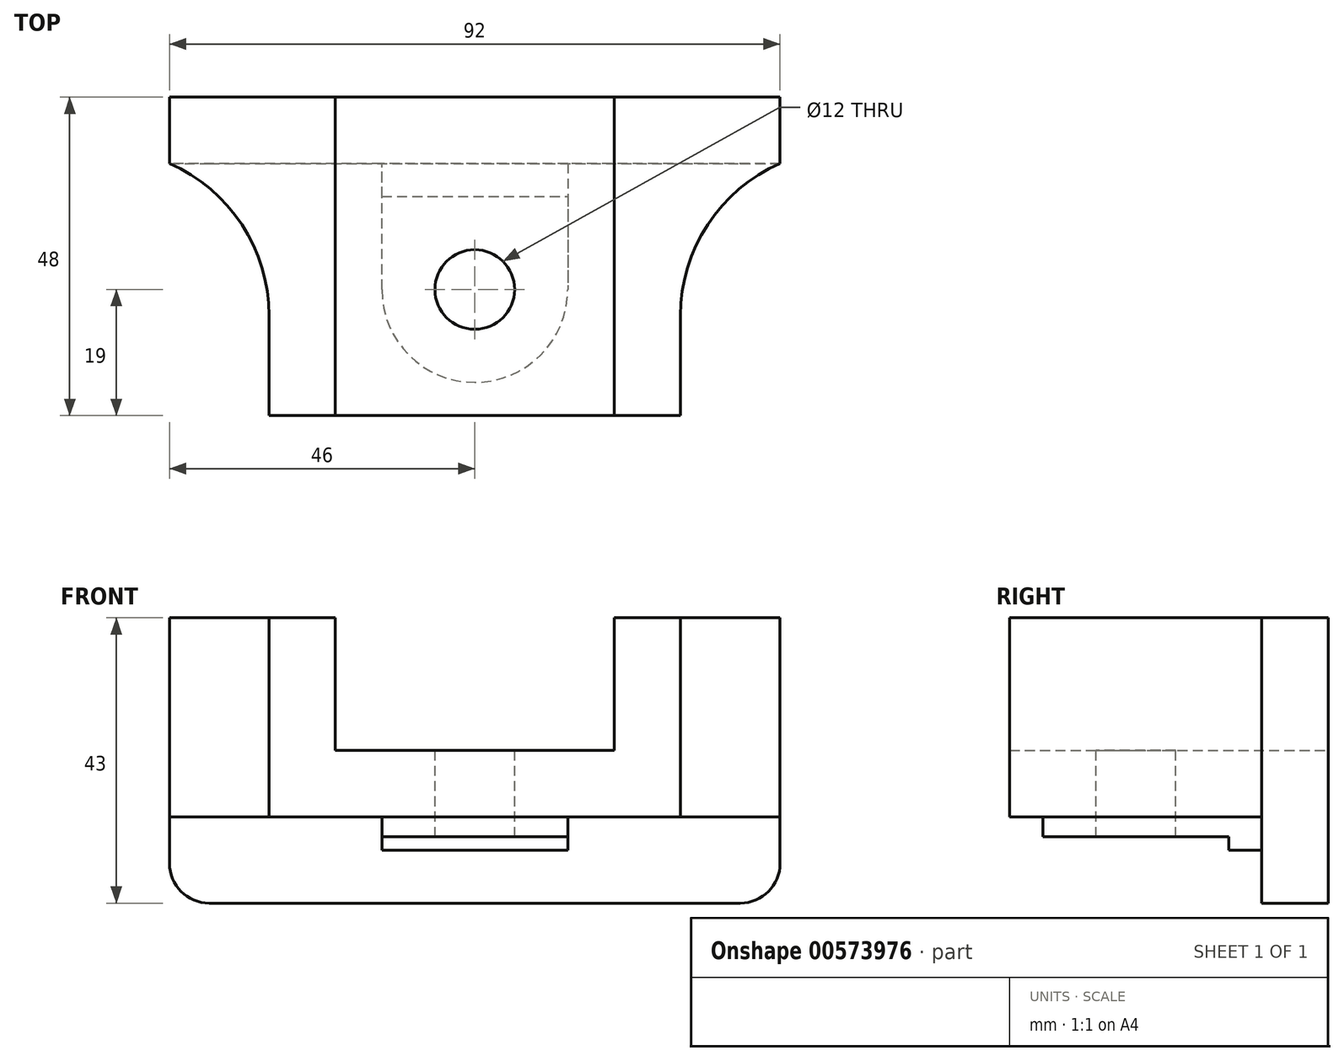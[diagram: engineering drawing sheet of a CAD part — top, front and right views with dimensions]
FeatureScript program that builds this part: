
annotation { "Feature Type Name" : "Feature", "Feature Type Description" : "" }
export const myFeature = defineFeature(function(context is Context, id is Id, definition is map)
    precondition{}
    {
        {
            var Q0;
            Q0=qCreatedBy(makeId("Front.planeOp"),FACE);
            var sketch = newSketch(context, id + "F0", { "sketchPlane" : qUnion([Q0])});
            skLineSegment(sketch, "E0", {"start": v(-46, 43) * mm, "end": v(-46, 0) * mm});
            skLineSegment(sketch, "E1", {"start": v(-46, 0) * mm, "end": v(46, 0) * mm});
            skLineSegment(sketch, "E2", {"start": v(46, 0) * mm, "end": v(46, 43) * mm});
            skLineSegment(sketch, "E3", {"start": v(46, 43) * mm, "end": v(31, 43) * mm});
            skLineSegment(sketch, "E4", {"start": v(31, 43) * mm, "end": v(31, 13) * mm});
            skLineSegment(sketch, "E5", {"start": v(31, 13) * mm, "end": v(-31, 13) * mm});
            skLineSegment(sketch, "E6", {"start": v(-31, 13) * mm, "end": v(-31, 43) * mm});
            skLineSegment(sketch, "E7", {"start": v(-31, 43) * mm, "end": v(-46, 43) * mm});
            skLineSegment(sketch, "E8", {"start": v(-31, 43) * mm, "end": v(-21, 43) * mm});
            skLineSegment(sketch, "E9", {"start": v(-21, 43) * mm, "end": v(-21, 23) * mm});
            skLineSegment(sketch, "E10", {"start": v(-21, 23) * mm, "end": v(21, 23) * mm});
            skLineSegment(sketch, "E11", {"start": v(21, 23) * mm, "end": v(21, 43) * mm});
            skLineSegment(sketch, "E12", {"start": v(21, 43) * mm, "end": v(31, 43) * mm});
            skSolve(sketch);
        }
        {
            var Q0;
            Q0=makeQuery(id+"F0.imprint","IMPRINT",FACE,{"disambiguationData":[TD([[makeQuery(id+"F0.imprint","IMPRINT",EDGE,{"derivedFrom":sQuery(id+"F0.wireOp",EDGE,"E4")}),-1.0]])]});
            extrude(context, id + "F1", {"entities" : qUnion([Q0]), "depth" : 48 * mm, "offsetDistance" : 25 * mm});
        }
        {
            var Q0;
            Q0 = qSketchRegion(id + "F0", true);
            extrude(context, id + "F2", {"entities" : qUnion([Q0]), "operationType" : NewBodyOperationType.ADD, "depth" : 10 * mm, "offsetDistance" : 25 * mm});
        }
        {
            var Q0;
            Q0=makeQuery(id+"F2.opExtrude","SWEPT_EDGE",EDGE,{"disambiguationData":[OSD([sQuery(id+"F0.wireOp",EDGE,"E0"),sQuery(id+"F0.wireOp",EDGE,"E1")])]});
            var Q1;
            Q1=makeQuery(id+"F2.opExtrude","SWEPT_EDGE",EDGE,{"disambiguationData":[OSD([sQuery(id+"F0.wireOp",EDGE,"E1"),sQuery(id+"F0.wireOp",EDGE,"E2")])]});
            fillet(context, id + "F3", {"entities" : qUnion([Q0, Q1]), "radius" : 6 * mm, "tangentPropagation" : true, "allowEdgeOverflow" : false});
        }
        {
            var Q0;
            Q0=makeQuery(id+"F2.boolean.opBoolean","INTERSECT",EDGE,{"derivedFrom":[makeQuery(id+"F1.opExtrude","SWEPT_FACE",FACE,{"disambiguationData":[OSD([sQuery(id+"F0.wireOp",EDGE,"E6")])]}),makeQuery(id+"F2.opExtrude","CAP_FACE",FACE,{"disambiguationData":[OSD([sQuery(id+"F0.wireOp",EDGE,"E0"),sQuery(id+"F0.wireOp",EDGE,"E1"),sQuery(id+"F0.wireOp",EDGE,"E2"),sQuery(id+"F0.wireOp",EDGE,"E3"),sQuery(id+"F0.wireOp",EDGE,"E7"),sQuery(id+"F0.wireOp",EDGE,"E8"),sQuery(id+"F0.wireOp",EDGE,"E9"),sQuery(id+"F0.wireOp",EDGE,"E10"),sQuery(id+"F0.wireOp",EDGE,"E11"),sQuery(id+"F0.wireOp",EDGE,"E12")])],"isStart":false})]});
            var Q1;
            Q1=makeQuery(id+"F2.boolean.opBoolean","INTERSECT",EDGE,{"derivedFrom":[makeQuery(id+"F1.opExtrude","SWEPT_FACE",FACE,{"disambiguationData":[OSD([sQuery(id+"F0.wireOp",EDGE,"E4")])]}),makeQuery(id+"F2.opExtrude","CAP_FACE",FACE,{"disambiguationData":[OSD([sQuery(id+"F0.wireOp",EDGE,"E0"),sQuery(id+"F0.wireOp",EDGE,"E1"),sQuery(id+"F0.wireOp",EDGE,"E2"),sQuery(id+"F0.wireOp",EDGE,"E3"),sQuery(id+"F0.wireOp",EDGE,"E7"),sQuery(id+"F0.wireOp",EDGE,"E8"),sQuery(id+"F0.wireOp",EDGE,"E9"),sQuery(id+"F0.wireOp",EDGE,"E10"),sQuery(id+"F0.wireOp",EDGE,"E11"),sQuery(id+"F0.wireOp",EDGE,"E12")])],"isStart":false})]});
            fillet(context, id + "F4", {"entities" : qUnion([Q0, Q1]), "radius" : 25 * mm, "tangentPropagation" : true, "allowEdgeOverflow" : false});
        }
        {
            var Q0;
            Q0=makeQuery(id+"F1.opExtrude","SWEPT_FACE",FACE,{"disambiguationData":[OSD([sQuery(id+"F0.wireOp",EDGE,"E5")])]});
            var sketch = newSketch(context, id + "F5", { "sketchPlane" : qUnion([Q0])});
            skArc(sketch, "E13", {"start": v(14, 29) * mm, "mid": v(0, 43) * mm, "end": v(-14, 29) * mm});
            skCircle(sketch, "E14", {"center": v(0, 29) * mm, "radius": 6 * mm});
            skLineSegment(sketch, "E15", {"start": v(-14, 29) * mm, "end": v(-14, 10) * mm});
            skLineSegment(sketch, "E16", {"start": v(-14, 10) * mm, "end": v(14, 10) * mm});
            skLineSegment(sketch, "E17", {"start": v(14, 10) * mm, "end": v(14, 29) * mm});
            skLineSegment(sketch, "E18", {"start": v(-14, 15) * mm, "end": v(14, 15) * mm});
            skSolve(sketch);
        }
        {
            var Q0;
            {var subQ1=sQuery(id+"F5.wireOp",EDGE,"E13");Q0=makeQuery(id+"F5.imprint","IMPRINT",FACE,{"disambiguationData":[TD([[makeQuery(id+"F5.imprint","IMPRINT",EDGE,{"derivedFrom":subQ1}),1.0]])]});}
            extrude(context, id + "F6", {"entities" : qUnion([Q0]), "operationType" : NewBodyOperationType.ADD, "depth" : 3 * mm, "offsetDistance" : 25 * mm});
        }
        {
            var Q0;
            {var subQ0=sQuery(id+"F5.wireOp",EDGE,"E16");Q0=makeQuery(id+"F5.imprint","IMPRINT",FACE,{"disambiguationData":[TD([[makeQuery(id+"F5.imprint","IMPRINT",EDGE,{"derivedFrom":subQ0}),-1.0]])]});}
            extrude(context, id + "F7", {"entities" : qUnion([Q0]), "operationType" : NewBodyOperationType.ADD, "depth" : 5 * mm, "offsetDistance" : 25 * mm});
        }
        {
            var Q0;
            Q0=makeQuery(id+"F5.imprint","IMPRINT",FACE,{"disambiguationData":[TD([[makeQuery(id+"F5.imprint","IMPRINT",EDGE,{"derivedFrom":sQuery(id+"F5.wireOp",EDGE,"E14")}),1.0]])]});
            extrude(context, id + "F8", {"entities" : qUnion([Q0]), "operationType" : NewBodyOperationType.REMOVE, "oppositeDirection" : true, "depth" : 25 * mm, "offsetDistance" : 25 * mm});
        }
    });
